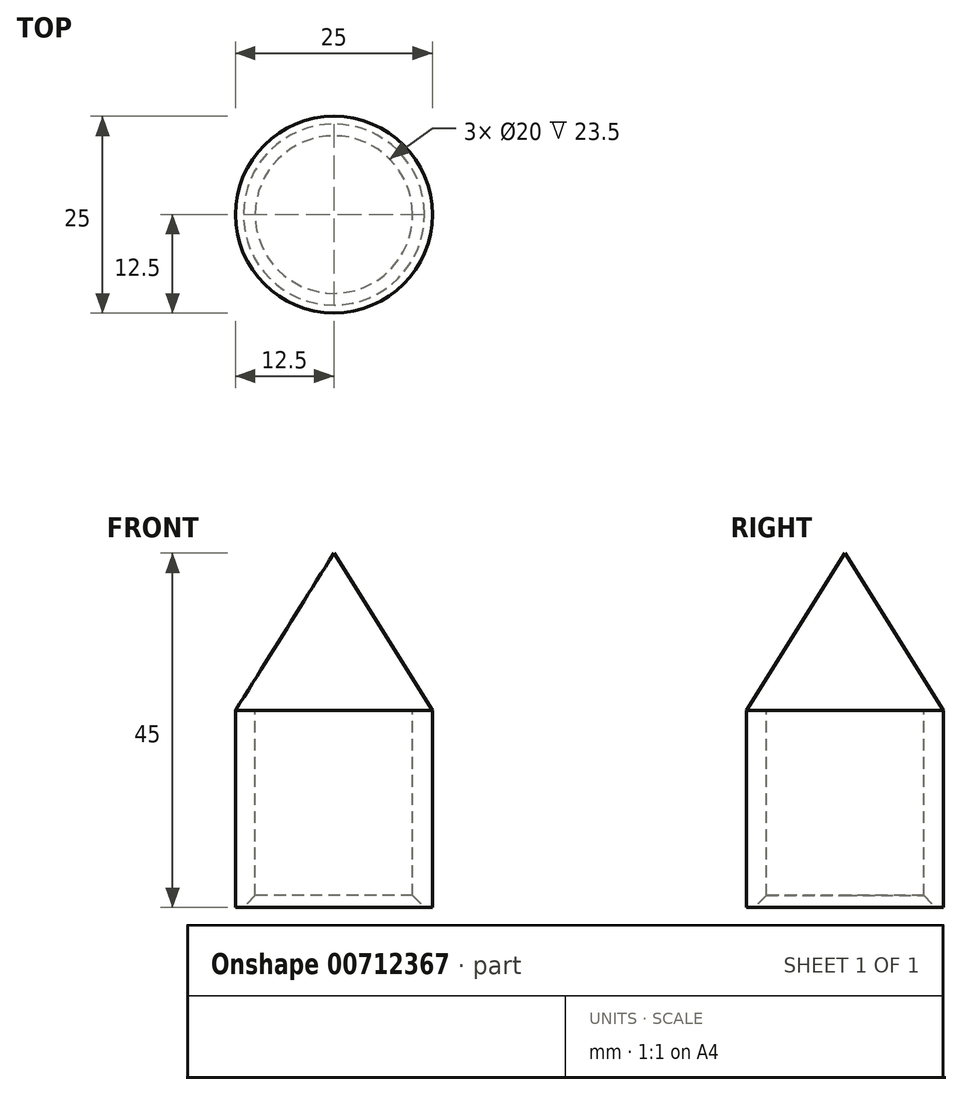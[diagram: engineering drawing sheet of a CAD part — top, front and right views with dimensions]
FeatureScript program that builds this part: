
annotation { "Feature Type Name" : "Feature", "Feature Type Description" : "" }
export const myFeature = defineFeature(function(context is Context, id is Id, definition is map)
    precondition{}
    {
        {
            var Q0;
            Q0=qCreatedBy(makeId("Front.planeOp"),FACE);
            var sketch = newSketch(context, id + "F0", { "sketchPlane" : qUnion([Q0])});
            skLineSegment(sketch, "E0", {"start": v(0, 0) * mm, "end": v(0, 45) * mm});
            skLineSegment(sketch, "E1.bottom", {"start": v(0, 0) * mm, "end": v(-10, 0) * mm});
            skLineSegment(sketch, "E1.top", {"start": v(0, 25) * mm, "end": v(-10, 25) * mm});
            skLineSegment(sketch, "E1.left", {"start": v(0, 0) * mm, "end": v(0, 25) * mm});
            skLineSegment(sketch, "E1.right", {"start": v(-10, 0) * mm, "end": v(-10, 25) * mm});
            skLineSegment(sketch, "E2", {"start": v(0, 0) * mm, "end": v(-12.5, 0) * mm});
            skLineSegment(sketch, "E3", {"start": v(-12.5, 25) * mm, "end": v(-12.5, 0) * mm});
            skLineSegment(sketch, "E4", {"start": v(-12.5, 25) * mm, "end": v(0, 45) * mm});
            skLineSegment(sketch, "E5", {"start": v(0, 45) * mm, "end": v(0, -22.21) * mm});
            skSolve(sketch);
        }
        {
            var Q0;
            {var subQ3=sQuery(id+"F0.wireOp",EDGE,"E1.top");Q0=makeQuery(id+"F0.imprint","IMPRINT",FACE,{"disambiguationData":[TD([[makeQuery(id+"F0.imprint","IMPRINT",EDGE,{"derivedFrom":subQ3}),-1.0]])]});}
            var Q1;
            Q1=sQuery(id+"F0.wireOp",EDGE,"E5");
            revolve(context, id + "F1", {"surfaceOperationType" : NewSurfaceOperationType.NEW, "entities" : qUnion([Q0]), "axis" : qUnion([Q1]), "revolveType" : RevolveType.FULL});
        }
        {
            var Q0;
            Q0=makeQuery(id+"F1.opRevolve","SWEPT_EDGE",EDGE,{"disambiguationData":[OSD([sQuery(id+"F0.wireOp",EDGE,"E1.right"),sQuery(id+"F0.wireOp",EDGE,"E2")])]});
            chamfer(context, id + "F2", {"entities" : qUnion([Q0]), "width" : 1.5 * mm, "tangentPropagation" : true});
        }
    });
